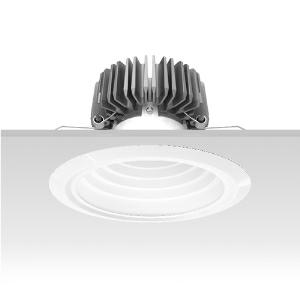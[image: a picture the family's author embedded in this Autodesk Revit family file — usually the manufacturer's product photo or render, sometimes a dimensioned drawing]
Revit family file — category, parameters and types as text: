
# Revit family: 3f_filippi_-_3f_reno_bianco_ampio_3f_filippi_-_30650_a01025_-_3f_reno_200_wh_2000-930_ep_wide___vt_wh_9ca8
name_source: partatom
category: Lighting Fixtures
units: mm (PartAtom-declared; Revit-internal decimal feet)

## family parameters
Cut with Voids When Loaded = No
Host = Face
Light Source = No
Part Type = Normal
Room Calculation Point = No
Round Connector Dimension = Use Diameter
Shared = No

## types (1)
- 3F Filippi - 3F Reno Bianco Ampio (1 x LED, 1804 lm, 25 W, 3000 K)
    Apparent Load = 25 VA
    Approval mark = ENEC
    CIE Flux Codes = 75 94 99 100 100
    Color Rendering = 90
    Color Temperature = 3000 K
    Control Gear = Electronic ballast
    Default Elevation = 1800 mm
    Description = ILLUMINOTECHNICAL
Luminous efficiency 100% (DLOR 100%, ULOR 0%).
Initial luminous flux of the luminaire 1804 lm.
Emergency luminaire luminous flux BLF 16.7%.
Direct symmetric wide distribution.
Installation Interdistance Transv.D = 1.56 x hu - Long.D = 1.56 x hu.
Average luminance <3000 cd/m² for radial angles >65°.
Tabular UGR (CIE 117 - 4H-8H; S=0.25H; 70/50/20): RUG 20.6 - 20.5.
Beam angle: 74° - 74°.
Luminous efficacy 72 lm/W.
Lifetime (L90/B10): 30000 h. (tq+25°C)
Lifetime (L85/B10): 50000 h. (tq+25°C)
Lifetime (L70/B10): 80000 h. (tq+25°C)
Sudden decreased luminous flux after 50000 hours: 0% (C0).
Photobiological safety in compliance with IEC/TR 62778: RG0 risk exempt, (IEC 62471).
In compliance with IEC/EN 62722-2-1 - IEC/EN 62717 standards.

SOURCE
Compact LED module 2000/930.
Energy efficiency class (UE 2019/2020 - UE 2019/2015): E.
CIE 13.3 Colour rendering index: CRI >90 (R9 >50%).
IES TM-30 Fidelity Index: Rf = 92 Rg = 101.
CCT nominal colour temperature 3000 K.
Colour initial tolerance (MacAdam): SDCM 3.
Zhaga Book 3 compliant.

MECHANICAL
Passive heat dissipator in die-casting aluminium, oversized, for optimum thermal management of the LED module.
Parabolic element with graduated/concentric rings in white polycarbonate.
Transparent external lens with glossy and satin differentiated surfaces, with a cooling and anti-insect system in methacrylate (PMMA).
Fastening spring clips in stainless steel.
Dimensions: diameter 226 mm, height 146 mm. Weight 1.615 kg.
IP44 protection degree for exposed part, IP20 for recessed part.
Mechanical strength to impacts IK06 (1 joule).
Glow-wire test resistance 650°C.

ELECTRICAL
Wiring on a separate unit.
Halogen Free electronic wiring 230V-50/60Hz, power factor 0.90, THD <25%, constant output current, SELV, class II, 1 driver.
Power of the luminaire 25 W.
CE - IEC 60598-1 - EN 60598-1.
EP maintained emergency wiring on board, 1h duration, 24h recharge; compliant with EN 60598-2-22, excluding high risk areas.
SAFE FLICKER: PstLM=<1 and SVM=<0.4 (IEC TR 61547-1 and IEC TR 63158), to ensure a more comfortable and safe light.
Ambient temperature from +5°C to +25°C.
Temperature class T6 max 85°C.
Relative humidity UR: <85%.

INSTALLATION
Pull-up recessed fitting.
False ceiling carving: 200 mm.
All accessories dedicated to this product are available on the Catalog and on our website www.3F-Filippi.com.

ACCESSORIES
A01025 - VT transparent glass, tempered, not flammable, locked and in line with the trim, in white polycarbonate.

APPLICATIONS
Environments: architectural, commercial, exhibition areas, transit areas, corridors, shops, display windows, service areas.
In false ceilings with narrow voids.

WARNING
Luminaire designed for disposal/recycling at end-of-life.
Replaceable (LED only) light source by a professional. Replaceable control gear by a professional.
    Height = 0 mm  [stored 0 ft]
    Lamp = 1 x LED
    Lamp Light Flux = 1804 lm
    Lamp Power = 25 W
    Lamp count = 1
    Length = 226 mm
    Lifetime = 50000 h
    Luminous efficacy = 72 lm/W
    Manufacturer = 3F Filippi
    ModVariant = No
    Model = 3F Filippi - 30650+A01025 - 3F Reno 200 WH 2000-930 EP WIDE + VT WH
    Mounting Place = Ceiling
    Mounting Type = Recessed
    Number of Poles = 1
    OnlyDefault = Yes
    Power Factor = 1
    Product Name = 3F Filippi - 3F Reno Bianco Ampio
    Product group = recessed luminaire
    ProductGroupID = 4
    Protection Class = Protection class II
    Protection Degree = IP 20
    RLX_Detail_Level = 1
    RLX_Emergency_Light_Flux = 0 lm
    RLX_Emergency_Type = 0
    RLX_Emergency_Type_DB = No
    RlxData = <blob elided: 95369 chars, md5=5b229706>
    Socket = socket
    Standby Power = 0 W
    System Light Flux = 1804 lm
    System Power = 25 W
    Type Comments = Product without accessories
    Type Image = 3ffilippi_3f_reno_200_wh__a01025.jpg
    URL = http://relux.com
    VarID = ---
    Voltage = 0 V
    Weight = 0.00 kg
    Width = 0 mm  [stored 0 ft]

note: [stored X ft] marks values corroborated as IEEE doubles in the binary element streams (Revit-internal decimal feet)

## geometry (parser evidence)
native form markers: Blend x4, Sweep x10
no freeform markers — native parametric forms only
